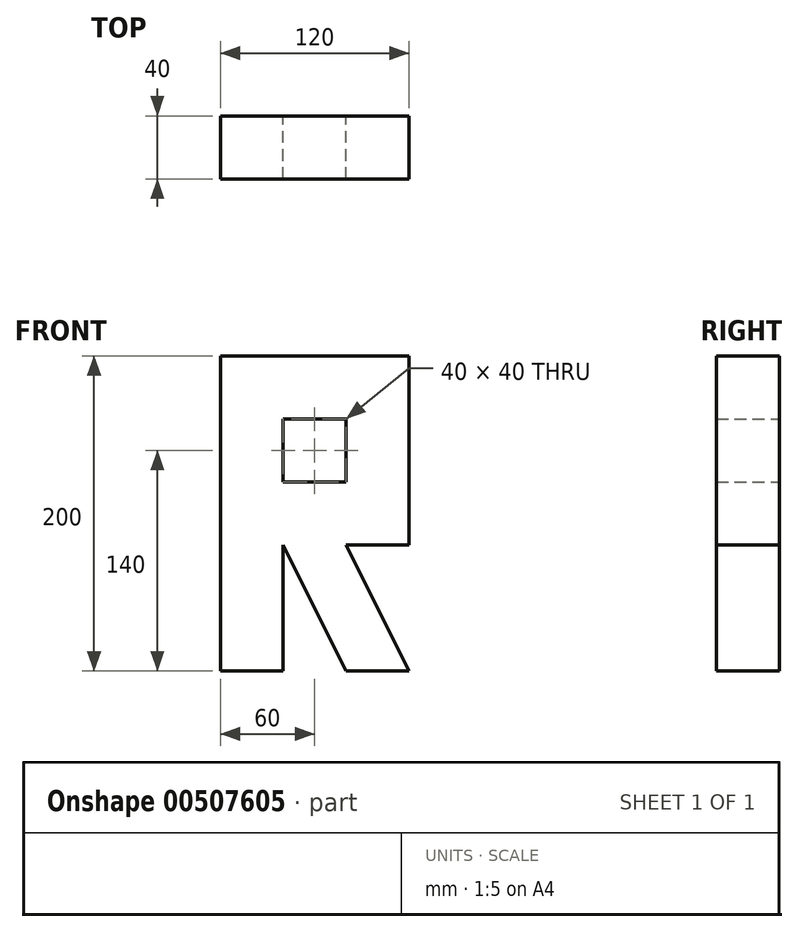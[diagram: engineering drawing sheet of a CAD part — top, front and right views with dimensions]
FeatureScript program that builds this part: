
annotation { "Feature Type Name" : "Feature", "Feature Type Description" : "" }
export const myFeature = defineFeature(function(context is Context, id is Id, definition is map)
    precondition{}
    {
        {
            var Q0;
            Q0=qCreatedBy(makeId("Front.planeOp"),FACE);
            var sketch = newSketch(context, id + "F0", { "sketchPlane" : qUnion([Q0])});
            skLineSegment(sketch, "E0.bottom", {"start": v(60, 100) * mm, "end": v(-60, 100) * mm});
            skLineSegment(sketch, "E0.top", {"start": v(60, -100) * mm, "end": v(-60, -100) * mm});
            skLineSegment(sketch, "E0.left", {"start": v(60, 100) * mm, "end": v(60, -100) * mm});
            skLineSegment(sketch, "E0.right", {"start": v(-60, 100) * mm, "end": v(-60, -100) * mm});
            skPoint(sketch, "E0.middle", {"position": v(0, 0) * mm});
            skLineSegment(sketch, "E1", {"start": v(-20, 100) * mm, "end": v(-20, -100) * mm});
            skLineSegment(sketch, "E2", {"start": v(20, 100) * mm, "end": v(20, -100) * mm});
            skLineSegment(sketch, "E3", {"start": v(60, 60) * mm, "end": v(-60, 60) * mm});
            skLineSegment(sketch, "E4", {"start": v(60, 20) * mm, "end": v(-60, 20) * mm});
            skLineSegment(sketch, "E5", {"start": v(60, -20) * mm, "end": v(-60, -20) * mm});
            skLineSegment(sketch, "E6", {"start": v(60, -60) * mm, "end": v(-60, -60) * mm});
            skLineSegment(sketch, "E7", {"start": v(20, -100) * mm, "end": v(-20, -20) * mm});
            skLineSegment(sketch, "E8", {"start": v(20, -20) * mm, "end": v(60, -100) * mm});
            skSolve(sketch);
        }
        {
            var Q0;
            {var subQ0=sQuery(id+"F0.wireOp",EDGE,"E0.right");var subQ1=sQuery(id+"F0.wireOp",EDGE,"E0.bottom");var subQ2=makeQuery(id+"F0.imprint","INTERSECT",VERTEX,{"derivedFrom":[subQ1,subQ0]});Q0=makeQuery(id+"F0.imprint","IMPRINT",FACE,{"disambiguationData":[TD([[makeQuery(id+"F0.imprint","IMPRINT",EDGE,{"disambiguationData":[TD([[subQ2,1.0]])],"derivedFrom":subQ1}),1.0]])]});}
            var Q1;
            {var subQ0=sQuery(id+"F0.wireOp",EDGE,"E1");var subQ1=sQuery(id+"F0.wireOp",EDGE,"E0.bottom");var subQ2=makeQuery(id+"F0.imprint","INTERSECT",VERTEX,{"derivedFrom":[subQ1,subQ0]});Q1=makeQuery(id+"F0.imprint","IMPRINT",FACE,{"disambiguationData":[TD([[makeQuery(id+"F0.imprint","IMPRINT",EDGE,{"disambiguationData":[TD([[subQ2,1.0]])],"derivedFrom":subQ1}),1.0]])]});}
            var Q2;
            {var subQ0=sQuery(id+"F0.wireOp",EDGE,"E0.left");var subQ1=sQuery(id+"F0.wireOp",EDGE,"E0.bottom");var subQ2=makeQuery(id+"F0.imprint","INTERSECT",VERTEX,{"derivedFrom":[subQ1,subQ0]});Q2=makeQuery(id+"F0.imprint","IMPRINT",FACE,{"disambiguationData":[TD([[makeQuery(id+"F0.imprint","IMPRINT",EDGE,{"disambiguationData":[TD([[subQ2,-1.0]])],"derivedFrom":subQ1}),1.0]])]});}
            var Q3;
            {var subQ0=sQuery(id+"F0.wireOp",EDGE,"E3");var subQ1=sQuery(id+"F0.wireOp",EDGE,"E0.left");var subQ2=makeQuery(id+"F0.imprint","INTERSECT",VERTEX,{"derivedFrom":[subQ1,subQ0]});Q3=makeQuery(id+"F0.imprint","IMPRINT",FACE,{"disambiguationData":[TD([[makeQuery(id+"F0.imprint","IMPRINT",EDGE,{"disambiguationData":[TD([[subQ2,-1.0]])],"derivedFrom":subQ1}),-1.0]])]});}
            var Q4;
            {var subQ0=sQuery(id+"F0.wireOp",EDGE,"E4");var subQ1=sQuery(id+"F0.wireOp",EDGE,"E0.left");var subQ2=makeQuery(id+"F0.imprint","INTERSECT",VERTEX,{"derivedFrom":[subQ1,subQ0]});Q4=makeQuery(id+"F0.imprint","IMPRINT",FACE,{"disambiguationData":[TD([[makeQuery(id+"F0.imprint","IMPRINT",EDGE,{"disambiguationData":[TD([[subQ2,-1.0]])],"derivedFrom":subQ1}),-1.0]])]});}
            var Q5;
            {var subQ1=sQuery(id+"F0.wireOp",EDGE,"E1");var subQ3=sQuery(id+"F0.wireOp",EDGE,"E4");var subQ4=makeQuery(id+"F0.imprint","INTERSECT",VERTEX,{"derivedFrom":[subQ1,subQ3]});Q5=makeQuery(id+"F0.imprint","IMPRINT",FACE,{"disambiguationData":[TD([[makeQuery(id+"F0.imprint","IMPRINT",EDGE,{"disambiguationData":[TD([[subQ4,1.0]])],"derivedFrom":subQ3}),1.0]])]});}
            var Q6;
            {var subQ0=sQuery(id+"F0.wireOp",EDGE,"E4");var subQ1=sQuery(id+"F0.wireOp",EDGE,"E0.right");var subQ2=makeQuery(id+"F0.imprint","INTERSECT",VERTEX,{"derivedFrom":[subQ1,subQ0]});Q6=makeQuery(id+"F0.imprint","IMPRINT",FACE,{"disambiguationData":[TD([[makeQuery(id+"F0.imprint","IMPRINT",EDGE,{"disambiguationData":[TD([[subQ2,-1.0]])],"derivedFrom":subQ1}),1.0]])]});}
            var Q7;
            {var subQ0=sQuery(id+"F0.wireOp",EDGE,"E5");var subQ1=sQuery(id+"F0.wireOp",EDGE,"E0.right");var subQ2=makeQuery(id+"F0.imprint","INTERSECT",VERTEX,{"derivedFrom":[subQ1,subQ0]});Q7=makeQuery(id+"F0.imprint","IMPRINT",FACE,{"disambiguationData":[TD([[makeQuery(id+"F0.imprint","IMPRINT",EDGE,{"disambiguationData":[TD([[subQ2,-1.0]])],"derivedFrom":subQ1}),1.0]])]});}
            var Q8;
            {var subQ0=sQuery(id+"F0.wireOp",EDGE,"E0.right");var subQ1=sQuery(id+"F0.wireOp",EDGE,"E0.top");var subQ2=makeQuery(id+"F0.imprint","INTERSECT",VERTEX,{"derivedFrom":[subQ1,subQ0]});Q8=makeQuery(id+"F0.imprint","IMPRINT",FACE,{"disambiguationData":[TD([[makeQuery(id+"F0.imprint","IMPRINT",EDGE,{"disambiguationData":[TD([[subQ2,1.0]])],"derivedFrom":subQ1}),-1.0]])]});}
            var Q9;
            {var subQ0=sQuery(id+"F0.wireOp",EDGE,"E3");var subQ1=sQuery(id+"F0.wireOp",EDGE,"E0.right");var subQ2=makeQuery(id+"F0.imprint","INTERSECT",VERTEX,{"derivedFrom":[subQ1,subQ0]});Q9=makeQuery(id+"F0.imprint","IMPRINT",FACE,{"disambiguationData":[TD([[makeQuery(id+"F0.imprint","IMPRINT",EDGE,{"disambiguationData":[TD([[subQ2,-1.0]])],"derivedFrom":subQ1}),1.0]])]});}
            var Q10;
            {var subQ1=sQuery(id+"F0.wireOp",EDGE,"E2");var subQ3=sQuery(id+"F0.wireOp",EDGE,"E6");var subQ4=makeQuery(id+"F0.imprint","INTERSECT",VERTEX,{"derivedFrom":[subQ1,subQ3]});Q10=makeQuery(id+"F0.imprint","IMPRINT",FACE,{"disambiguationData":[TD([[makeQuery(id+"F0.imprint","IMPRINT",EDGE,{"disambiguationData":[TD([[subQ4,-1.0]])],"derivedFrom":subQ3}),-1.0]])]});}
            var Q11;
            {var subQ3=sQuery(id+"F0.wireOp",EDGE,"E2");var subQ5=sQuery(id+"F0.wireOp",EDGE,"E6");var subQ7=makeQuery(id+"F0.imprint","INTERSECT",VERTEX,{"derivedFrom":[subQ3,subQ5]});Q11=makeQuery(id+"F0.imprint","IMPRINT",FACE,{"disambiguationData":[TD([[makeQuery(id+"F0.imprint","IMPRINT",EDGE,{"disambiguationData":[TD([[subQ7,1.0]])],"derivedFrom":subQ5}),1.0]])]});}
            var Q12;
            {var subQ1=sQuery(id+"F0.wireOp",EDGE,"E2");var subQ3=sQuery(id+"F0.wireOp",EDGE,"E6");var subQ4=makeQuery(id+"F0.imprint","INTERSECT",VERTEX,{"derivedFrom":[subQ1,subQ3]});Q12=makeQuery(id+"F0.imprint","IMPRINT",FACE,{"disambiguationData":[TD([[makeQuery(id+"F0.imprint","IMPRINT",EDGE,{"disambiguationData":[TD([[subQ4,-1.0]])],"derivedFrom":subQ3}),1.0]])]});}
            var Q13;
            {var subQ1=sQuery(id+"F0.wireOp",EDGE,"E2");var subQ3=sQuery(id+"F0.wireOp",EDGE,"E6");var subQ4=makeQuery(id+"F0.imprint","INTERSECT",VERTEX,{"derivedFrom":[subQ1,subQ3]});Q13=makeQuery(id+"F0.imprint","IMPRINT",FACE,{"disambiguationData":[TD([[makeQuery(id+"F0.imprint","IMPRINT",EDGE,{"disambiguationData":[TD([[subQ4,1.0]])],"derivedFrom":subQ3}),-1.0]])]});}
            extrude(context, id + "F1", {"entities" : qUnion([Q0, Q1, Q2, Q3, Q4, Q5, Q6, Q7, Q8, Q9, Q10, Q11, Q12, Q13]), "depth" : 40 * mm, "offsetDistance" : 25 * mm});
        }
    });
